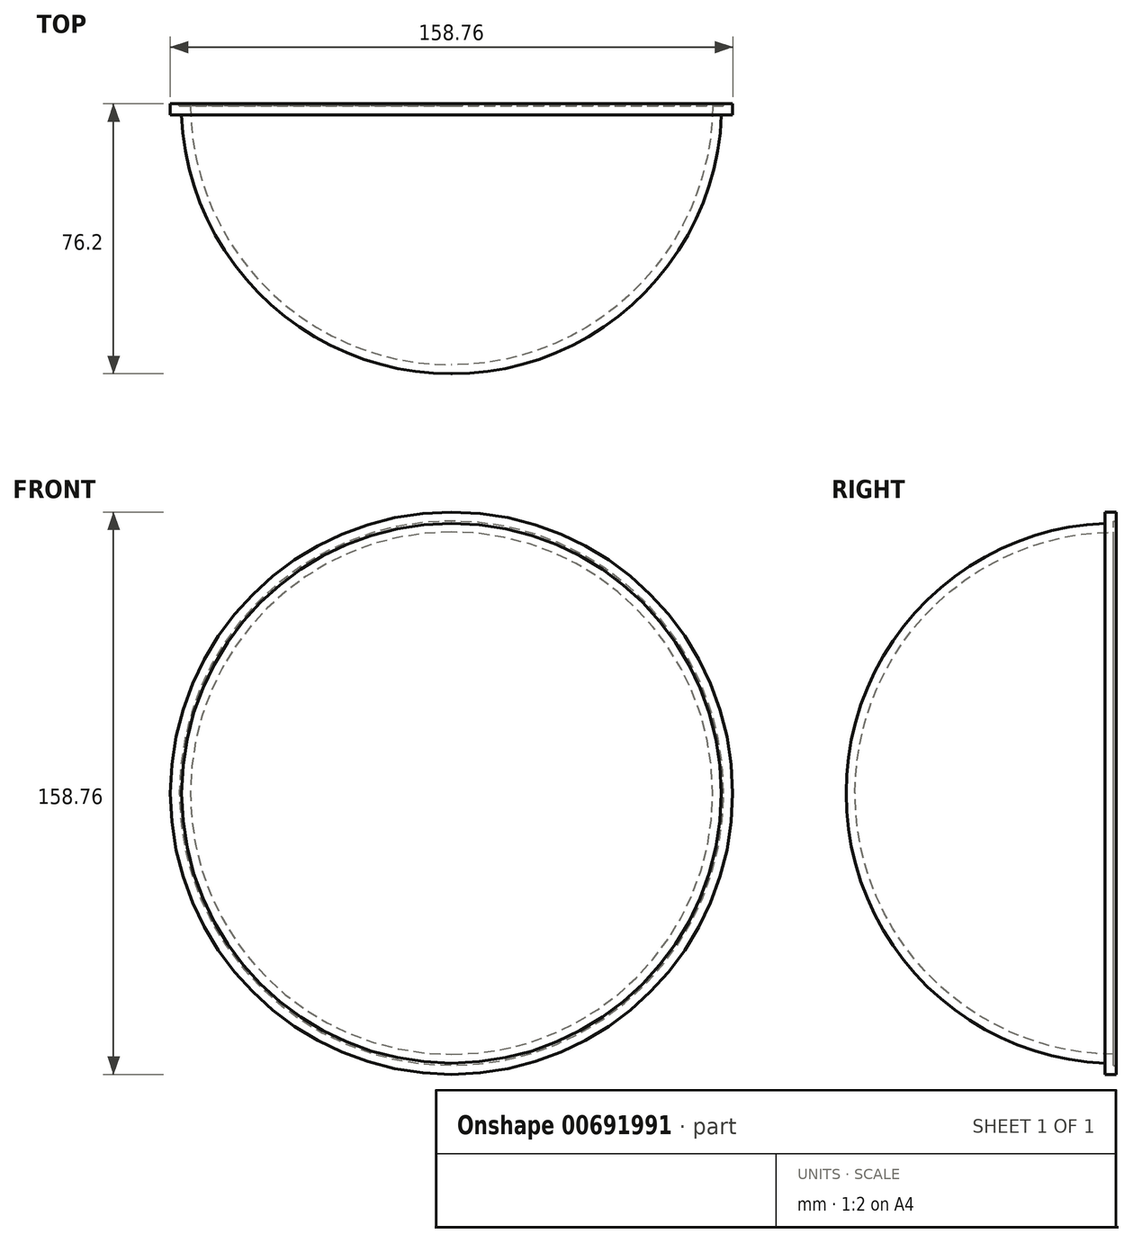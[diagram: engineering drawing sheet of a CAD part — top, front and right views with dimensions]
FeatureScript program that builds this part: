
annotation { "Feature Type Name" : "Feature", "Feature Type Description" : "" }
export const myFeature = defineFeature(function(context is Context, id is Id, definition is map)
    precondition{}
    {
        {
            var Q0;
            Q0=qCreatedBy(makeId("Front.planeOp"),FACE);
            var sketch = newSketch(context, id + "F0", { "sketchPlane" : qUnion([Q0])});
            skCircle(sketch, "E0", {"center": v(0, 0) * mm, "radius": 76.2 * mm});
            skCircle(sketch, "E1", {"center": v(0, 0) * mm, "radius": 79.38 * mm});
            skSolve(sketch);
        }
        {
            var Q0;
            Q0=makeQuery(id+"F0.imprint","IMPRINT",FACE,{"disambiguationData":[TD([[makeQuery(id+"F0.imprint","IMPRINT",EDGE,{"derivedFrom":sQuery(id+"F0.wireOp",EDGE,"E0")}),1.0]])]});
            extrude(context, id + "F1", {"entities" : qUnion([Q0]), "depth" : 76.2 * mm, "offsetDistance" : 25.4 * mm});
        }
        {
            var Q0;
            Q0=makeQuery(id+"F0.imprint","IMPRINT",FACE,{"disambiguationData":[TD([[makeQuery(id+"F0.imprint","IMPRINT",EDGE,{"derivedFrom":sQuery(id+"F0.wireOp",EDGE,"E0")}),-1.0]])]});
            extrude(context, id + "F2", {"entities" : qUnion([Q0]), "operationType" : NewBodyOperationType.ADD, "depth" : 3.17 * mm, "offsetDistance" : 25.4 * mm});
        }
        {
            var Q0;
            Q0=makeQuery(id+"F1.opExtrude","CAP_EDGE",EDGE,{"disambiguationData":[OSD([sQuery(id+"F0.wireOp",EDGE,"E0")])],"isStart":false});
            fillet(context, id + "F3", {"entities" : qUnion([Q0]), "tangentPropagation" : true, "radius" : 76.2 * mm, "defaultsChanged" : true, "vertexSettings" : [], "allowEdgeOverflow" : false});
        }
        {
            var Q0;
            {var subQ0=sQuery(id+"F0.wireOp",EDGE,"E0");Q0=makeQuery(id+"F2.boolean.opBoolean","MERGE",FACE,{"derivedFrom":[makeQuery(id+"F1.opExtrude","CAP_FACE",FACE,{"disambiguationData":[OSD([subQ0])],"isStart":true}),makeQuery(id+"F2.opExtrude","CAP_FACE",FACE,{"disambiguationData":[OSD([subQ0,sQuery(id+"F0.wireOp",EDGE,"E1")])],"isStart":true})]});}
            shell(context, id + "F4", {"entities" : qUnion([Q0]), "thickness" : 2.54 * mm});
        }
    });
